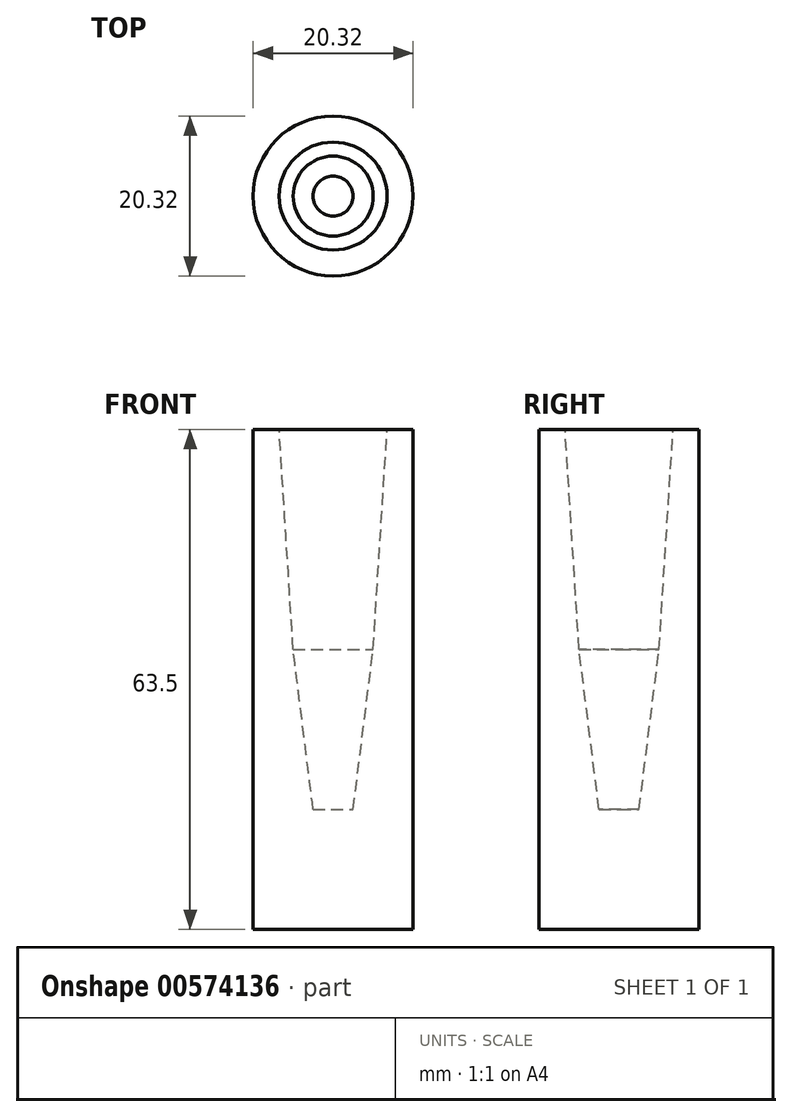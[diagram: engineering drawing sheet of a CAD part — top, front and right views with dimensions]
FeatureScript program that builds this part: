
annotation { "Feature Type Name" : "Feature", "Feature Type Description" : "" }
export const myFeature = defineFeature(function(context is Context, id is Id, definition is map)
    precondition{}
    {
        {
            var Q0;
            Q0=qCreatedBy(makeId("Front.planeOp"),FACE);
            var sketch = newSketch(context, id + "F0", { "sketchPlane" : qUnion([Q0])});
            skLineSegment(sketch, "E0.bottom", {"start": v(0, 0) * mm, "end": v(10.16, 0) * mm});
            skLineSegment(sketch, "E0.top", {"start": v(6.86, 63.5) * mm, "end": v(10.16, 63.5) * mm});
            skLineSegment(sketch, "E0.left", {"start": v(0, 0) * mm, "end": v(0, 63.5) * mm, "construction": true});
            skLineSegment(sketch, "E0.right", {"start": v(10.16, 0) * mm, "end": v(10.16, 63.5) * mm});
            skLineSegment(sketch, "E1", {"start": v(2.54, 15.24) * mm, "end": v(0, 15.24) * mm});
            skLineSegment(sketch, "E2", {"start": v(6.86, 63.5) * mm, "end": v(5.08, 35.56) * mm});
            skLineSegment(sketch, "E3", {"start": v(5.08, 35.56) * mm, "end": v(2.54, 15.24) * mm});
            skLineSegment(sketch, "E4", {"start": v(0, 15.24) * mm, "end": v(0, 0) * mm});
            skSolve(sketch);
        }
        {
            var Q0;
            Q0=makeQuery(id+"F0.imprint","IMPRINT",FACE,{"disambiguationData":[TD([[makeQuery(id+"F0.imprint","IMPRINT",EDGE,{"derivedFrom":sQuery(id+"F0.wireOp",EDGE,"E0.bottom")}),1.0]])]});
            var Q1;
            Q1=sQuery(id+"F0.wireOp",EDGE,"E3");
            var Q2;
            Q2=sQuery(id+"F0.wireOp",EDGE,"E2");
            var Q3;
            Q3=sQuery(id+"F0.wireOp",EDGE,"E0.right");
            var Q4;
            Q4=sQuery(id+"F0.wireOp",EDGE,"E0.bottom");
            var Q5;
            Q5=sQuery(id+"F0.wireOp",EDGE,"E0.top");
            var Q6;
            Q6=sQuery(id+"F0.wireOp",EDGE,"E4");
            var Q7;
            Q7=sQuery(id+"F0.wireOp",EDGE,"E1");
            var Q8;
            Q8=sQuery(id+"F0.wireOp",EDGE,"E0.left");
            revolve(context, id + "F1", {"entities" : qUnion([Q0]), "surfaceEntities" : qUnion([Q1, Q2, Q3, Q4, Q5, Q6, Q7]), "axis" : qUnion([Q8]), "revolveType" : RevolveType.FULL});
        }
    });
